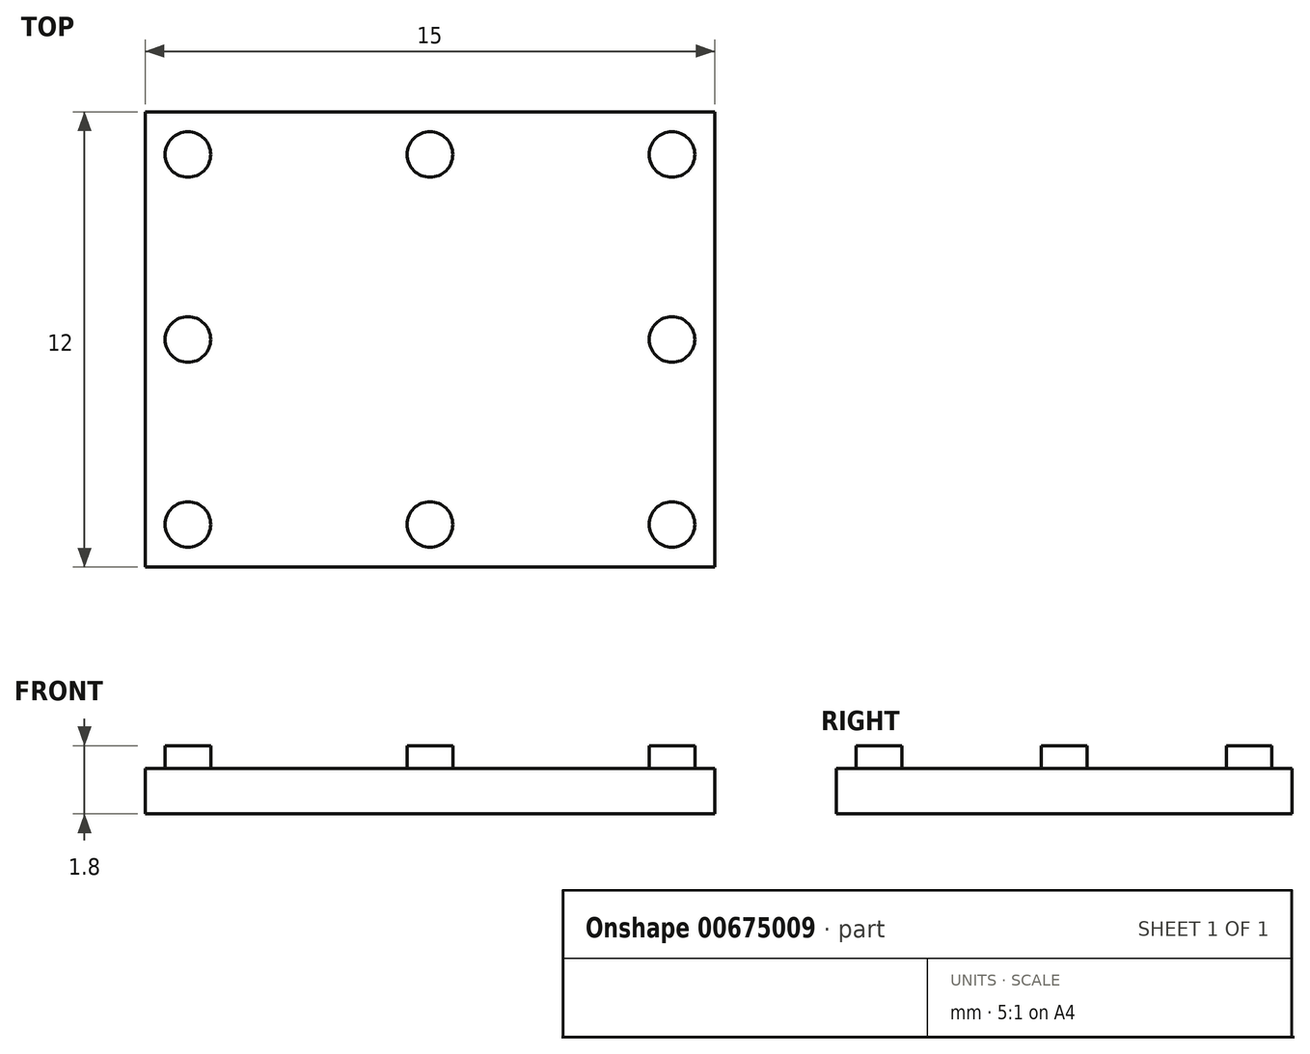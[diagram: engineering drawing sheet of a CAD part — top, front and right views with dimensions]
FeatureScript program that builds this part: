
annotation { "Feature Type Name" : "Feature", "Feature Type Description" : "" }
export const myFeature = defineFeature(function(context is Context, id is Id, definition is map)
    precondition{}
    {
        {
            assignVariable(context, id + "F0", {"name" : "Faktor", "anyValue" : 1.5});
        }
        {
            var Q0;
            Q0=qCreatedBy(makeId("Top.planeOp"),FACE);
            var sketch = newSketch(context, id + "F1", { "sketchPlane" : qUnion([Q0])});
            skLineSegment(sketch, "E0.bottom", {"start": v(-7.5, -6) * mm, "end": v(7.5, -6) * mm});
            skLineSegment(sketch, "E0.top", {"start": v(-7.5, 6) * mm, "end": v(7.5, 6) * mm});
            skLineSegment(sketch, "E0.left", {"start": v(-7.5, -6) * mm, "end": v(-7.5, 6) * mm});
            skLineSegment(sketch, "E0.right", {"start": v(7.5, -6) * mm, "end": v(7.5, 6) * mm});
            skPoint(sketch, "E0.middle", {"position": v(0, 0) * mm});
            skSolve(sketch);
        }
        {
            var Q0;
            Q0=qSketchRegion(id+"F1",true);
            extrude(context, id + "F2", {"entities" : qUnion([Q0]), "depth" : getVariable(context, 'Faktor') * 0.8 * mm, "offsetDistance" : 25 * mm});
        }
        {
            var Q0;
            Q0=makeQuery(id+"F2.opExtrude","CAP_FACE",FACE,{"disambiguationData":[OSD([sQuery(id+"F1.wireOp",EDGE,"E0.bottom"),sQuery(id+"F1.wireOp",EDGE,"E0.top"),sQuery(id+"F1.wireOp",EDGE,"E0.left"),sQuery(id+"F1.wireOp",EDGE,"E0.right")])],"isStart":false});
            var sketch = newSketch(context, id + "F3", { "sketchPlane" : qUnion([Q0])});
            skLineSegment(sketch, "E1.bottom", {"start": v(-6.38, 4.87) * mm, "end": v(6.37, 4.88) * mm, "construction": true});
            skLineSegment(sketch, "E1.top", {"start": v(-6.38, -4.88) * mm, "end": v(6.38, -4.87) * mm, "construction": true});
            skLineSegment(sketch, "E1.left", {"start": v(-6.38, 4.87) * mm, "end": v(-6.38, -4.88) * mm, "construction": true});
            skLineSegment(sketch, "E1.right", {"start": v(6.38, 4.88) * mm, "end": v(6.38, -4.87) * mm, "construction": true});
            skPoint(sketch, "E1.middle", {"position": v(0, 0) * mm});
            skCircle(sketch, "E2", {"center": v(-6.38, 4.87) * mm, "radius": 0.6 * mm});
            skCircle(sketch, "E3", {"center": v(-6.38, 0) * mm, "radius": 0.6 * mm});
            skCircle(sketch, "E4", {"center": v(-6.38, -4.88) * mm, "radius": 0.6 * mm});
            skCircle(sketch, "E5", {"center": v(0, 4.88) * mm, "radius": 0.6 * mm});
            skCircle(sketch, "E6", {"center": v(6.37, 4.88) * mm, "radius": 0.6 * mm});
            skCircle(sketch, "E7", {"center": v(6.38, 0) * mm, "radius": 0.6 * mm});
            skCircle(sketch, "E8", {"center": v(6.38, -4.87) * mm, "radius": 0.6 * mm});
            skCircle(sketch, "E9", {"center": v(0, -4.88) * mm, "radius": 0.6 * mm});
            skSolve(sketch);
        }
        {
            var Q0;
            Q0=qSketchRegion(id+"F3",true);
            extrude(context, id + "F4", {"entities" : qUnion([Q0]), "operationType" : NewBodyOperationType.ADD, "depth" : getVariable(context, 'Faktor') * 0.4 * mm, "offsetDistance" : 25 * mm});
        }
    });
